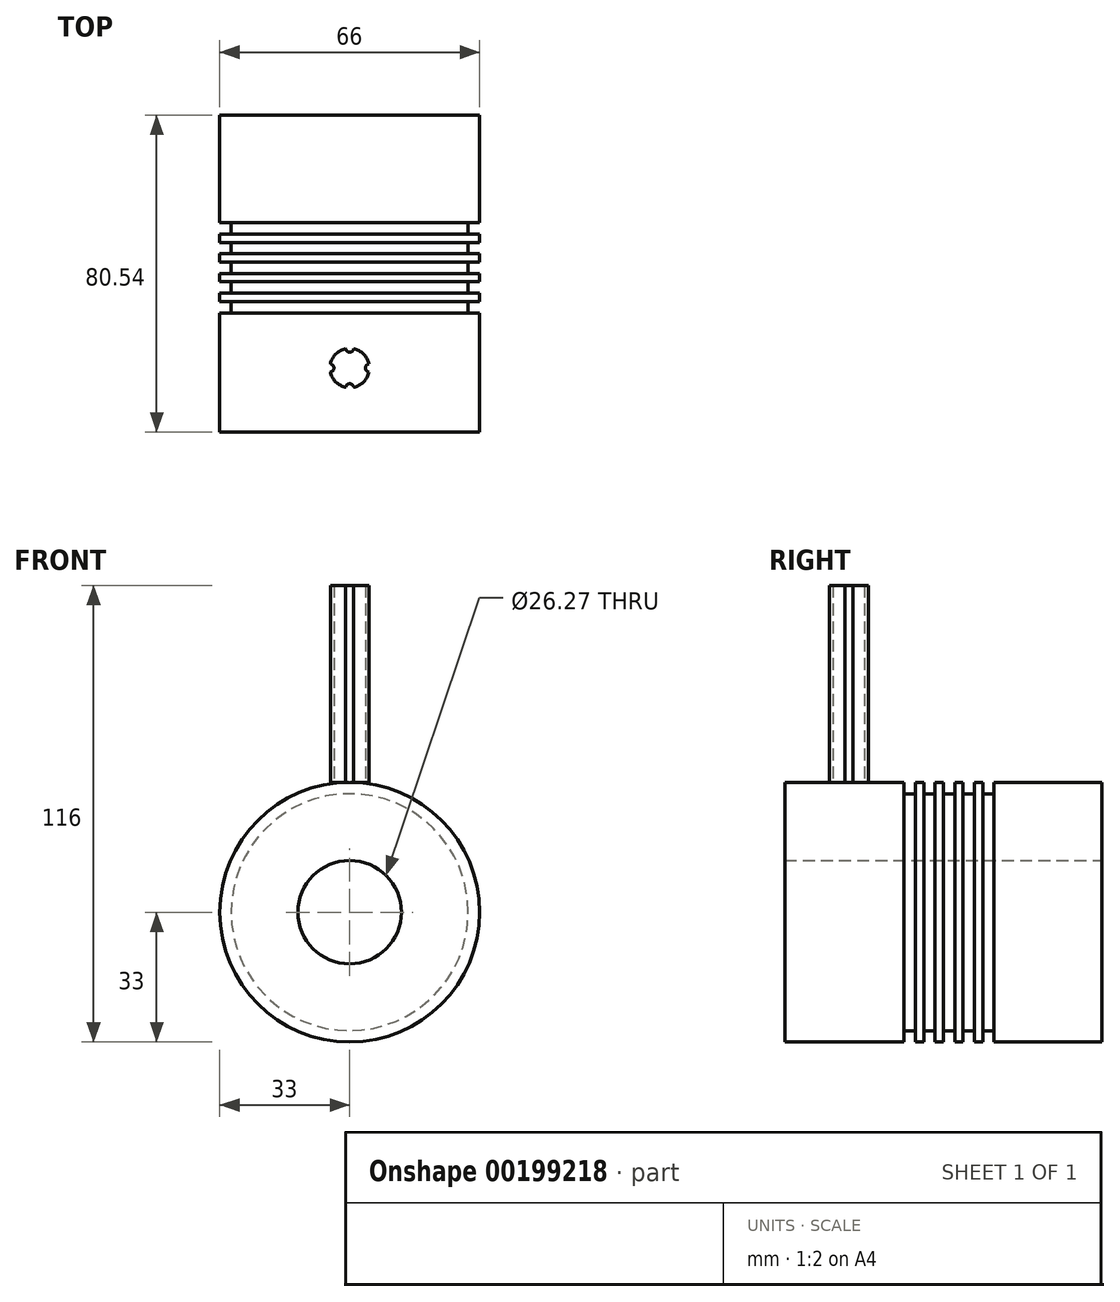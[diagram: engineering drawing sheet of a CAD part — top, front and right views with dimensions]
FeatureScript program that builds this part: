
annotation { "Feature Type Name" : "Feature", "Feature Type Description" : "" }
export const myFeature = defineFeature(function(context is Context, id is Id, definition is map)
    precondition{}
    {
        {
            var Q0;
            Q0=qCreatedBy(makeId("Top.planeOp"),FACE);
            var sketch = newSketch(context, id + "F0", { "sketchPlane" : qUnion([Q0])});
            skLineSegment(sketch, "E0.bottom", {"start": v(13.13, 40.27) * mm, "end": v(33, 40.27) * mm});
            skLineSegment(sketch, "E0.top", {"start": v(13.13, -40.27) * mm, "end": v(33, -40.27) * mm});
            skLineSegment(sketch, "E0.left", {"start": v(13.13, 40.27) * mm, "end": v(13.13, -40.27) * mm});
            skLineSegment(sketch, "E0.right", {"start": v(33, 40.27) * mm, "end": v(33, 12.9) * mm});
            skLineSegment(sketch, "E1", {"start": v(33, 0) * mm, "end": v(30.1, 0) * mm});
            skPoint(sketch, "E1.endSnap0", {"position": v(33, 0) * mm});
            skLineSegment(sketch, "E2", {"start": v(30.1, 0) * mm, "end": v(30.1, 2.9) * mm});
            skLineSegment(sketch, "E3", {"start": v(30.1, 2.9) * mm, "end": v(33, 2.9) * mm});
            skLineSegment(sketch, "E4.0.1.0", {"start": v(30.1, 5) * mm, "end": v(30.1, 7.9) * mm});
            skLineSegment(sketch, "E4.0.1.1", {"start": v(30.1, 7.9) * mm, "end": v(33, 7.9) * mm});
            skLineSegment(sketch, "E4.0.1.2", {"start": v(33, 5) * mm, "end": v(30.1, 5) * mm});
            skLineSegment(sketch, "E4.0.2.0", {"start": v(30.1, 10) * mm, "end": v(30.1, 12.9) * mm});
            skLineSegment(sketch, "E4.0.2.1", {"start": v(30.1, 12.9) * mm, "end": v(33, 12.9) * mm});
            skLineSegment(sketch, "E4.0.2.2", {"start": v(33, 10) * mm, "end": v(30.1, 10) * mm});
            skLineSegment(sketch, "E4.direction2", {"start": v(30.1, 0) * mm, "end": v(30.1, 5) * mm, "construction": true});
            skPoint(sketch, "E5.0.1.0", {"position": v(33, -5) * mm});
            skLineSegment(sketch, "E5.0.1.1", {"start": v(30.1, -2.1) * mm, "end": v(33, -2.1) * mm});
            skLineSegment(sketch, "E5.0.1.2", {"start": v(30.1, -5) * mm, "end": v(30.1, -2.1) * mm});
            skLineSegment(sketch, "E5.0.1.3", {"start": v(33, -5) * mm, "end": v(30.1, -5) * mm});
            skPoint(sketch, "E5.0.2.0", {"position": v(33, -10) * mm});
            skLineSegment(sketch, "E5.0.2.1", {"start": v(30.1, -7.1) * mm, "end": v(33, -7.1) * mm});
            skLineSegment(sketch, "E5.0.2.2", {"start": v(30.1, -10) * mm, "end": v(30.1, -7.1) * mm});
            skLineSegment(sketch, "E5.0.2.3", {"start": v(33, -10) * mm, "end": v(30.1, -10) * mm});
            skPoint(sketch, "E5.2.0.0", {"position": v(83, 0) * mm});
            skLineSegment(sketch, "E5.2.0.1", {"start": v(80.1, 2.9) * mm, "end": v(83, 2.9) * mm});
            skLineSegment(sketch, "E5.2.0.2", {"start": v(80.1, 0) * mm, "end": v(80.1, 2.9) * mm});
            skLineSegment(sketch, "E5.2.0.3", {"start": v(83, 0) * mm, "end": v(80.1, 0) * mm});
            skPoint(sketch, "E5.2.1.0", {"position": v(83, -5) * mm});
            skLineSegment(sketch, "E5.2.1.1", {"start": v(80.1, -2.1) * mm, "end": v(83, -2.1) * mm});
            skLineSegment(sketch, "E5.2.1.2", {"start": v(80.1, -5) * mm, "end": v(80.1, -2.1) * mm});
            skLineSegment(sketch, "E5.2.1.3", {"start": v(83, -5) * mm, "end": v(80.1, -5) * mm});
            skPoint(sketch, "E5.2.2.0", {"position": v(83, -10) * mm});
            skLineSegment(sketch, "E5.2.2.1", {"start": v(80.1, -7.1) * mm, "end": v(83, -7.1) * mm});
            skLineSegment(sketch, "E5.2.2.2", {"start": v(80.1, -10) * mm, "end": v(80.1, -7.1) * mm});
            skLineSegment(sketch, "E5.2.2.3", {"start": v(83, -10) * mm, "end": v(80.1, -10) * mm});
            skLineSegment(sketch, "E5.direction2", {"start": v(30.1, 0) * mm, "end": v(30.1, -5) * mm, "construction": true});
            skLineSegment(sketch, "E6.trimOffspring", {"start": v(33, 10) * mm, "end": v(33, 7.9) * mm});
            skLineSegment(sketch, "E7.trimOffspring", {"start": v(33, 5) * mm, "end": v(33, 2.9) * mm});
            skLineSegment(sketch, "E8.trimOffspring", {"start": v(33, 0) * mm, "end": v(33, -2.1) * mm});
            skLineSegment(sketch, "E9.trimOffspring", {"start": v(33, -5) * mm, "end": v(33, -7.1) * mm});
            skLineSegment(sketch, "E10.trimOffspring", {"start": v(33, -10) * mm, "end": v(33, -40.27) * mm});
            skLineSegment(sketch, "E11", {"start": v(0, 42.03) * mm, "end": v(0, -45) * mm, "construction": true});
            skSolve(sketch);
        }
        {
            var Q0;
            Q0=makeQuery(id+"F0.imprint","IMPRINT",FACE,{"disambiguationData":[TD([[makeQuery(id+"F0.imprint","IMPRINT",EDGE,{"derivedFrom":sQuery(id+"F0.wireOp",EDGE,"E0.bottom")}),-1.0]])]});
            var Q1;
            Q1=sQuery(id+"F0.wireOp",EDGE,"E11");
            revolve(context, id + "F1", {"entities" : qUnion([Q0]), "axis" : qUnion([Q1]), "revolveType" : RevolveType.FULL});
        }
        {
            var Q0;
            Q0=qCreatedBy(makeId("Top.planeOp"),FACE);
            cPlane(context, id + "F2", {"entities" : qUnion([Q0]), "cplaneType" : CPlaneType.OFFSET, "offset" : (65.99 / 2) * mm, "width" : 150 * mm, "height" : 150 * mm});
        }
        {
            var Q0;
            Q0=qCreatedBy(id+"F2.planeOp",FACE);
            var sketch = newSketch(context, id + "F3", { "sketchPlane" : qUnion([Q0])});
            skCircle(sketch, "E12", {"center": v(0, -24) * mm, "radius": 5 * mm});
            skCircle(sketch, "E13", {"center": v(5, -24) * mm, "radius": 1 * mm});
            skCircle(sketch, "E14", {"center": v(-5, -24) * mm, "radius": 1 * mm});
            skCircle(sketch, "E15", {"center": v(0, -19) * mm, "radius": 1 * mm});
            skCircle(sketch, "E16", {"center": v(0, -29) * mm, "radius": 1 * mm});
            skSolve(sketch);
        }
        {
            var Q0;
            {var subQ1=sQuery(id+"F3.wireOp",EDGE,"E12");var subQ9=sQuery(id+"F3.wireOp",EDGE,"E15");var subQ12=makeQuery(id+"F3.imprint","INTERSECT",VERTEX,{"disambiguationData":[OD(0.0)],"derivedFrom":[subQ1,subQ9]});Q0=makeQuery(id+"F3.imprint","IMPRINT",FACE,{"disambiguationData":[TD([[makeQuery(id+"F3.imprint","IMPRINT",EDGE,{"disambiguationData":[TD([[subQ12,1.0]])],"derivedFrom":subQ1}),1.0]])]});}
            extrude(context, id + "F4", {"entities" : qUnion([Q0]), "depth" : 50 * mm});
        }
    });
